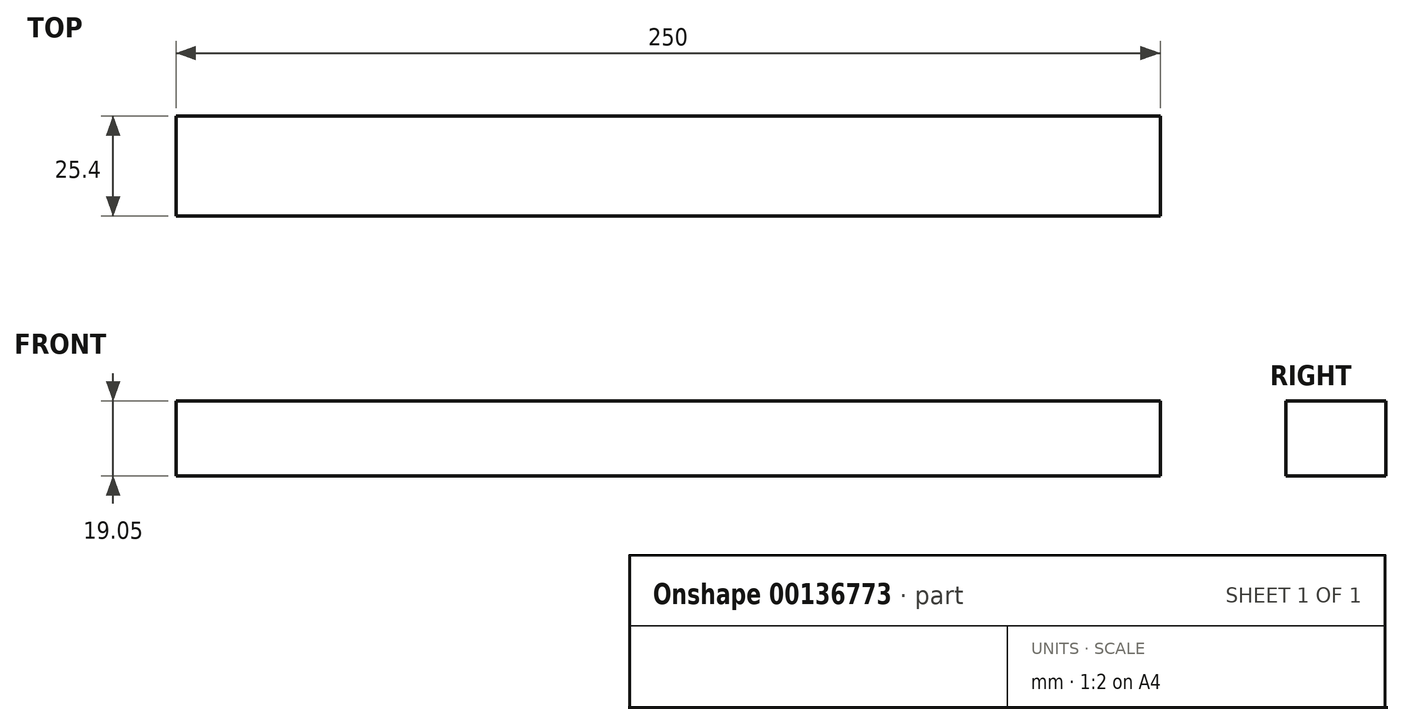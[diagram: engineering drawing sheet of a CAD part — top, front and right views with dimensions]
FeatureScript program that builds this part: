
annotation { "Feature Type Name" : "Feature", "Feature Type Description" : "" }
export const myFeature = defineFeature(function(context is Context, id is Id, definition is map)
    precondition{}
    {
        {
            var Q0;
            Q0=qCreatedBy(makeId("Front.planeOp"),FACE);
            var sketch = newSketch(context, id + "F0", { "sketchPlane" : qUnion([Q0])});
            skLineSegment(sketch, "E0.bottom", {"start": v(-138.16, -1.41) * mm, "end": v(111.84, -1.41) * mm});
            skLineSegment(sketch, "E0.top", {"start": v(-138.16, -20.46) * mm, "end": v(111.84, -20.46) * mm});
            skLineSegment(sketch, "E0.left", {"start": v(-138.16, -1.41) * mm, "end": v(-138.16, -20.46) * mm});
            skLineSegment(sketch, "E0.right", {"start": v(111.84, -1.41) * mm, "end": v(111.84, -20.46) * mm});
            skSolve(sketch);
        }
        {
            var Q0;
            Q0 = qSketchRegion(id + "F0", true);
            extrude(context, id + "F1", {"entities" : qUnion([Q0]), "depth" : 25.4 * mm});
        }
    });
